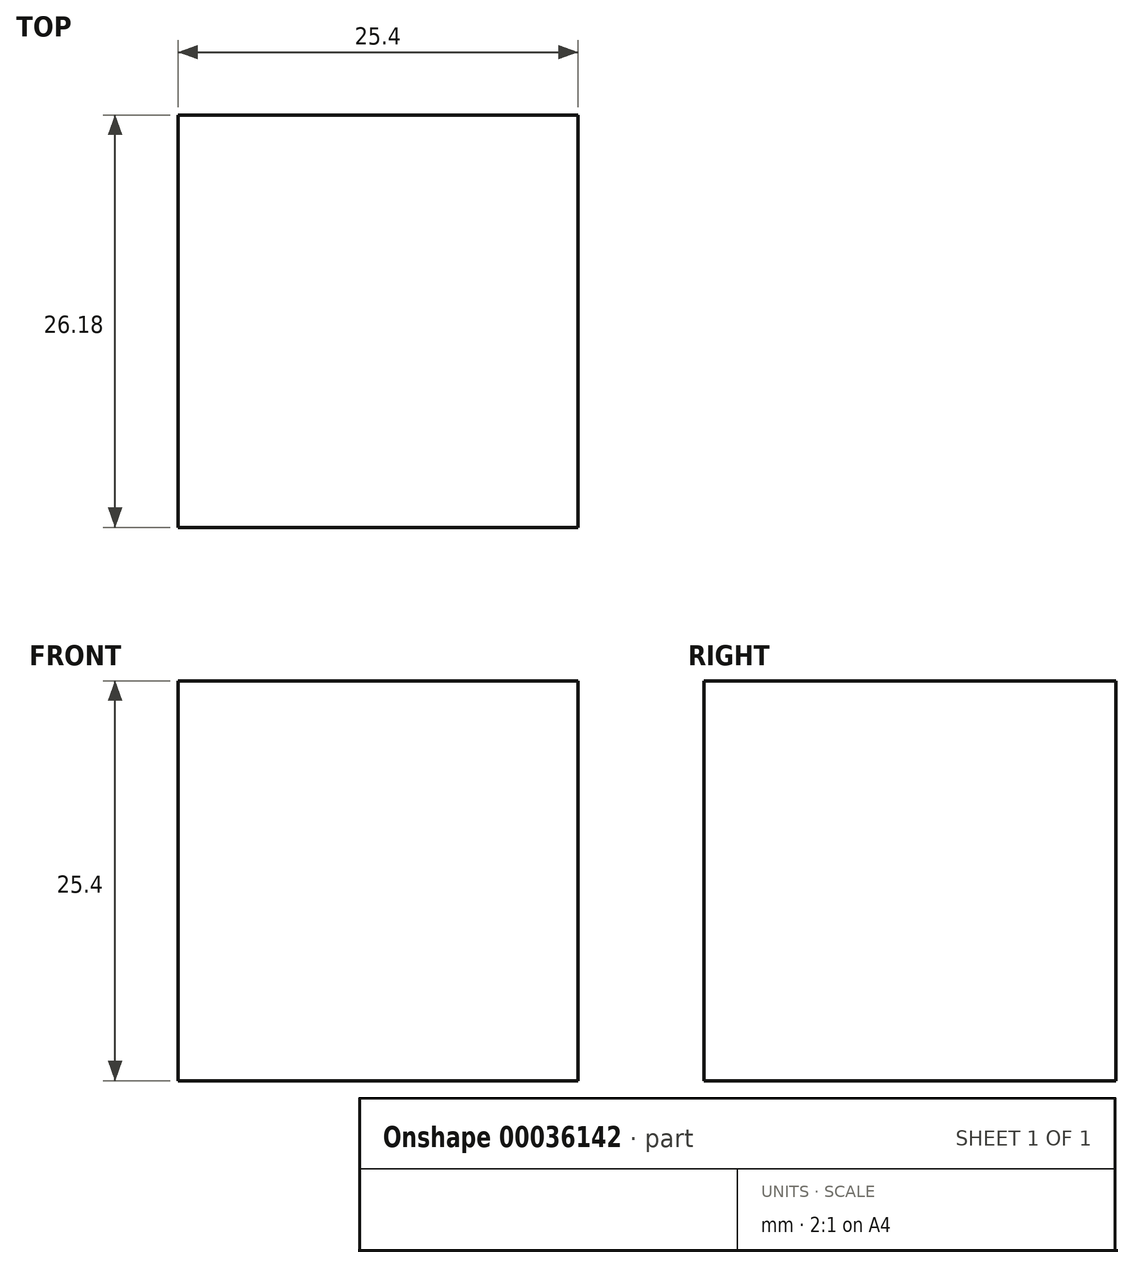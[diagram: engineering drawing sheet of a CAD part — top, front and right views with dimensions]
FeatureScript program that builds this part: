
annotation { "Feature Type Name" : "Feature", "Feature Type Description" : "" }
export const myFeature = defineFeature(function(context is Context, id is Id, definition is map)
    precondition{}
    {
        {
            var Q0;
            Q0=qCreatedBy(makeId("Top.planeOp"),FACE);
            var sketch = newSketch(context, id + "F0", { "sketchPlane" : qUnion([Q0])});
            skLineSegment(sketch, "E0.bottom", {"start": v(-12.24, 14.64) * mm, "end": v(13.16, 14.64) * mm});
            skLineSegment(sketch, "E0.top", {"start": v(-12.24, -11.54) * mm, "end": v(13.16, -11.54) * mm});
            skLineSegment(sketch, "E0.left", {"start": v(-12.24, 14.64) * mm, "end": v(-12.24, -11.54) * mm});
            skLineSegment(sketch, "E0.right", {"start": v(13.16, 14.64) * mm, "end": v(13.16, -11.54) * mm});
            skSolve(sketch);
        }
        {
            var Q0;
            Q0=makeQuery(id+"F0.imprint","IMPRINT",FACE,{"disambiguationData":[TD([[makeQuery(id+"F0.imprint","IMPRINT",EDGE,{"derivedFrom":sQuery(id+"F0.wireOp",EDGE,"E0.bottom")}),-1.0]])]});
            var Q1;
            Q1 = qConstructionFilter(qBodyType(qCreatedBy(id + "F0" ,EDGE), BodyType.WIRE), ConstructionObject.NO);
            extrude(context, id + "F1", {"entities" : qUnion([Q0]), "surfaceEntities" : qUnion([Q1]), "depth" : 25.4 * mm});
        }
    });
